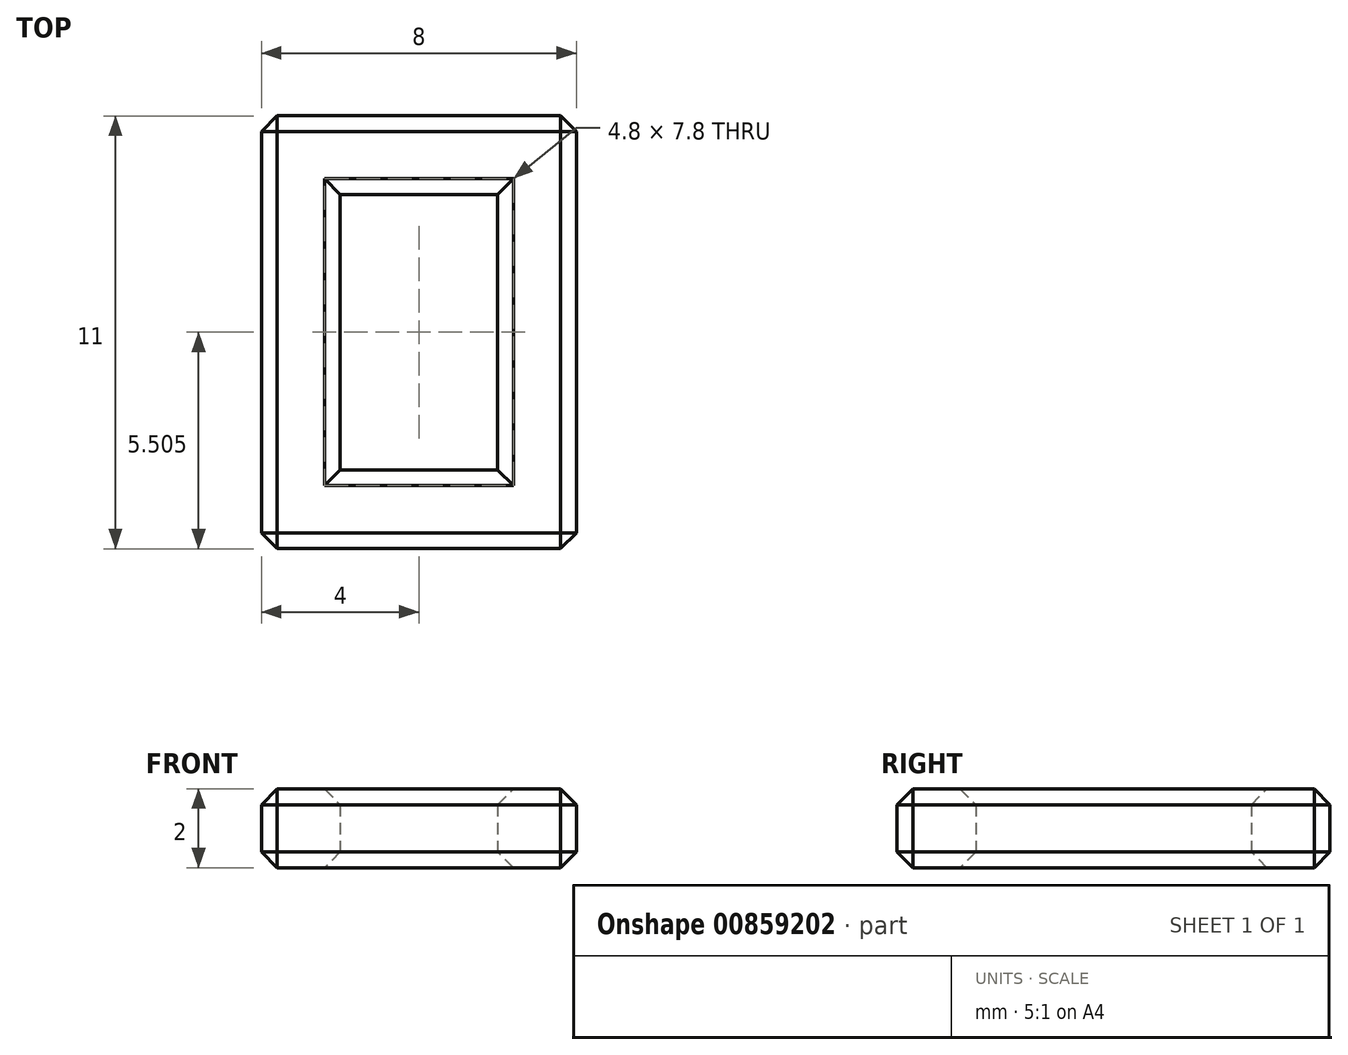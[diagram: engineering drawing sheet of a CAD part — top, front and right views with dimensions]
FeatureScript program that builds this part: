
annotation { "Feature Type Name" : "Feature", "Feature Type Description" : "" }
export const myFeature = defineFeature(function(context is Context, id is Id, definition is map)
    precondition{}
    {
        {
            var Q0;
            Q0=qCreatedBy(makeId("Top.planeOp"),FACE);
            var sketch = newSketch(context, id + "F0", { "sketchPlane" : qUnion([Q0])});
            skLineSegment(sketch, "E0.bottom", {"start": v(-14.33, -24.39) * mm, "end": v(-6.33, -24.39) * mm});
            skLineSegment(sketch, "E0.top", {"start": v(-14.33, -35.39) * mm, "end": v(-6.33, -35.39) * mm});
            skLineSegment(sketch, "E0.left", {"start": v(-14.33, -24.39) * mm, "end": v(-14.33, -35.39) * mm});
            skLineSegment(sketch, "E0.right", {"start": v(-6.33, -24.39) * mm, "end": v(-6.33, -35.39) * mm});
            skLineSegment(sketch, "E1.bottom", {"start": v(-12.33, -26.39) * mm, "end": v(-8.33, -26.39) * mm});
            skLineSegment(sketch, "E1.top", {"start": v(-12.33, -33.39) * mm, "end": v(-8.33, -33.39) * mm});
            skLineSegment(sketch, "E1.left", {"start": v(-12.33, -26.39) * mm, "end": v(-12.33, -33.39) * mm});
            skLineSegment(sketch, "E1.right", {"start": v(-8.33, -26.39) * mm, "end": v(-8.33, -33.39) * mm});
            skSolve(sketch);
        }
        {
            var Q0;
            Q0 = qSketchRegion(id + "F0", true);
            extrude(context, id + "F1", {"entities" : qUnion([Q0]), "depth" : 2 * mm, "offsetDistance" : 25 * mm});
        }
        {
            var Q0;
            Q0=makeQuery(id+"F1.opExtrude","CAP_EDGE",EDGE,{"disambiguationData":[OSD([sQuery(id+"F0.wireOp",EDGE,"E1.right")])],"isStart":false});
            var Q1;
            Q1=makeQuery(id+"F1.opExtrude","CAP_EDGE",EDGE,{"disambiguationData":[OSD([sQuery(id+"F0.wireOp",EDGE,"E1.top")])],"isStart":false});
            var Q2;
            Q2=makeQuery(id+"F1.opExtrude","CAP_EDGE",EDGE,{"disambiguationData":[OSD([sQuery(id+"F0.wireOp",EDGE,"E1.left")])],"isStart":false});
            var Q3;
            Q3=makeQuery(id+"F1.opExtrude","CAP_EDGE",EDGE,{"disambiguationData":[OSD([sQuery(id+"F0.wireOp",EDGE,"E1.bottom")])],"isStart":false});
            var Q4;
            Q4=makeQuery(id+"F1.opExtrude","CAP_EDGE",EDGE,{"disambiguationData":[OSD([sQuery(id+"F0.wireOp",EDGE,"E0.top")])],"isStart":false});
            var Q5;
            Q5=makeQuery(id+"F1.opExtrude","CAP_EDGE",EDGE,{"disambiguationData":[OSD([sQuery(id+"F0.wireOp",EDGE,"E0.left")])],"isStart":false});
            var Q6;
            Q6=makeQuery(id+"F1.opExtrude","SWEPT_EDGE",EDGE,{"disambiguationData":[OSD([sQuery(id+"F0.wireOp",EDGE,"E0.top"),sQuery(id+"F0.wireOp",EDGE,"E0.left")])]});
            var Q7;
            Q7=makeQuery(id+"F1.opExtrude","SWEPT_EDGE",EDGE,{"disambiguationData":[OSD([sQuery(id+"F0.wireOp",EDGE,"E0.top"),sQuery(id+"F0.wireOp",EDGE,"E0.right")])]});
            var Q8;
            Q8=makeQuery(id+"F1.opExtrude","CAP_EDGE",EDGE,{"disambiguationData":[OSD([sQuery(id+"F0.wireOp",EDGE,"E0.right")])],"isStart":false});
            var Q9;
            Q9=makeQuery(id+"F1.opExtrude","CAP_EDGE",EDGE,{"disambiguationData":[OSD([sQuery(id+"F0.wireOp",EDGE,"E0.bottom")])],"isStart":false});
            var Q10;
            Q10=makeQuery(id+"F1.opExtrude","SWEPT_EDGE",EDGE,{"disambiguationData":[OSD([sQuery(id+"F0.wireOp",EDGE,"E0.bottom"),sQuery(id+"F0.wireOp",EDGE,"E0.right")])]});
            var Q11;
            Q11=makeQuery(id+"F1.opExtrude","SWEPT_EDGE",EDGE,{"disambiguationData":[OSD([sQuery(id+"F0.wireOp",EDGE,"E0.bottom"),sQuery(id+"F0.wireOp",EDGE,"E0.left")])]});
            var Q12;
            Q12=makeQuery(id+"F1.opExtrude","CAP_EDGE",EDGE,{"disambiguationData":[OSD([sQuery(id+"F0.wireOp",EDGE,"E0.left")])],"isStart":true});
            var Q13;
            Q13=makeQuery(id+"F1.opExtrude","CAP_EDGE",EDGE,{"disambiguationData":[OSD([sQuery(id+"F0.wireOp",EDGE,"E1.left")])],"isStart":true});
            var Q14;
            Q14=makeQuery(id+"F1.opExtrude","CAP_EDGE",EDGE,{"disambiguationData":[OSD([sQuery(id+"F0.wireOp",EDGE,"E1.bottom")])],"isStart":true});
            var Q15;
            Q15=makeQuery(id+"F1.opExtrude","CAP_EDGE",EDGE,{"disambiguationData":[OSD([sQuery(id+"F0.wireOp",EDGE,"E0.bottom")])],"isStart":true});
            var Q16;
            Q16=makeQuery(id+"F1.opExtrude","CAP_EDGE",EDGE,{"disambiguationData":[OSD([sQuery(id+"F0.wireOp",EDGE,"E0.right")])],"isStart":true});
            var Q17;
            Q17=makeQuery(id+"F1.opExtrude","CAP_EDGE",EDGE,{"disambiguationData":[OSD([sQuery(id+"F0.wireOp",EDGE,"E1.right")])],"isStart":true});
            var Q18;
            Q18=makeQuery(id+"F1.opExtrude","CAP_EDGE",EDGE,{"disambiguationData":[OSD([sQuery(id+"F0.wireOp",EDGE,"E1.top")])],"isStart":true});
            var Q19;
            Q19=makeQuery(id+"F1.opExtrude","CAP_EDGE",EDGE,{"disambiguationData":[OSD([sQuery(id+"F0.wireOp",EDGE,"E0.top")])],"isStart":true});
            chamfer(context, id + "F2", {"entities" : qUnion([Q0, Q1, Q2, Q3, Q4, Q5, Q6, Q7, Q8, Q9, Q10, Q11, Q12, Q13, Q14, Q15, Q16, Q17, Q18, Q19]), "width" : .4 * mm, "tangentPropagation" : true});
        }
    });
